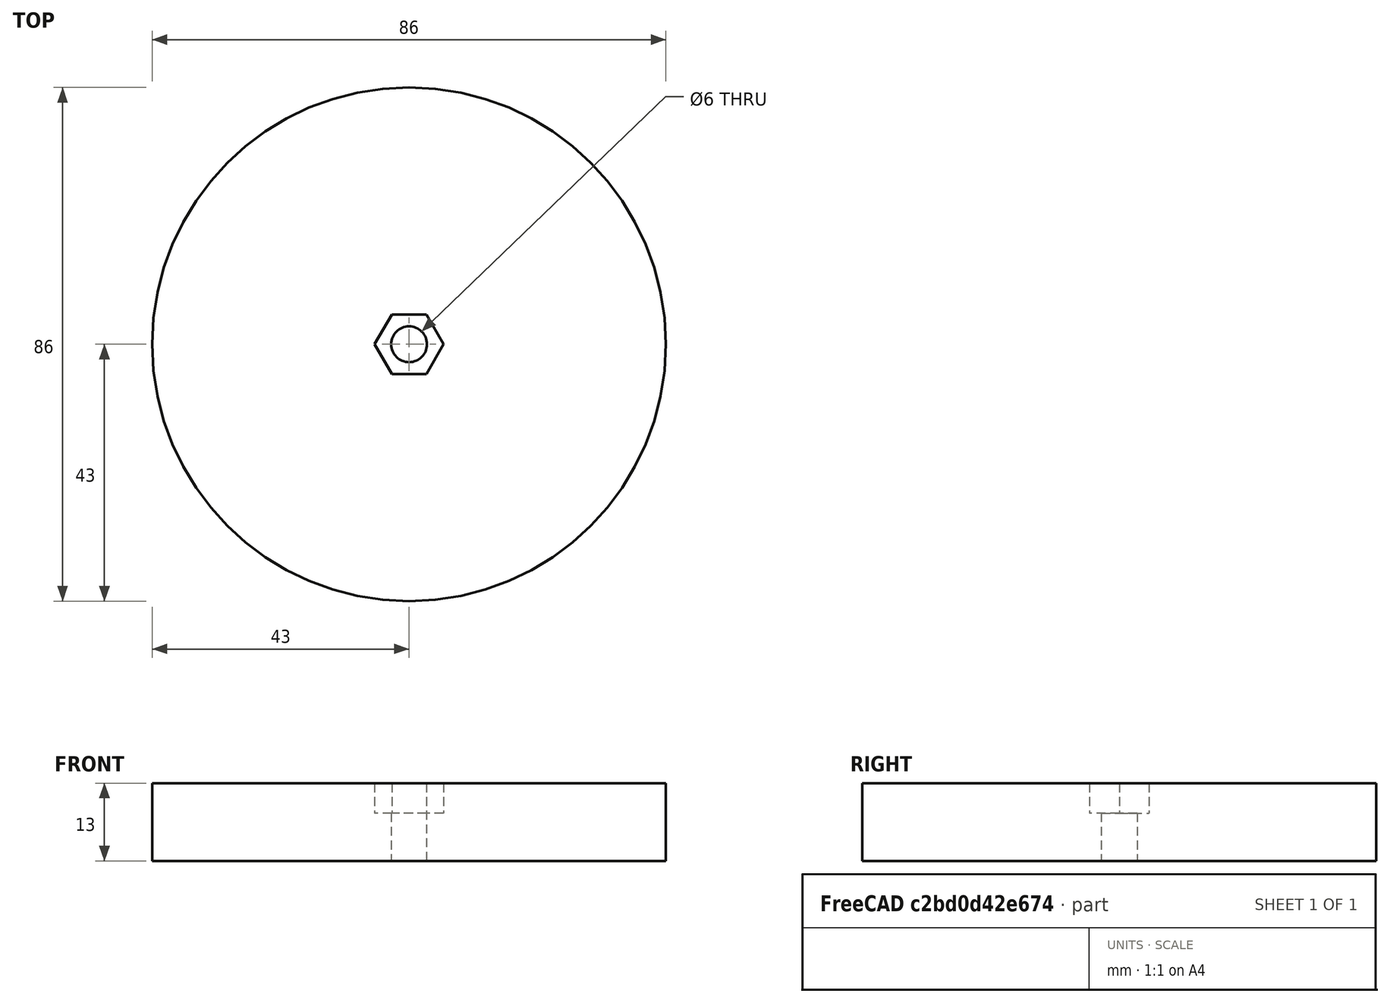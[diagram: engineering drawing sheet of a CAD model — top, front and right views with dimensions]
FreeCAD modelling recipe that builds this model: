
FCSTD DOCUMENT  (FreeCAD 0.18.4R)
Label: 12
License: All rights reserved
LicenseURL: http://en.wikipedia.org/wiki/All_rights_reserved
objects: Sketcher::SketchObject×2, PartDesign::Pad×1, PartDesign::Pocket×1, PartDesign::Body×1
note: 7 computed .brp shape members not serialized (recipe doc carries the construction recipe); baked Part::Feature solids carry a one-line shape summary decoded from their .brp

FEATURE [PartDesign::Pad] Pad  label="Unnamed"
  Length = 100
  Length2 = 100
  Type = 0
FEATURE [Sketcher::SketchObject] Sketch  label="Sketch001"
  MapMode = 5
  Placement = pos=(0,0,13) rot=(0,0,1;0rad)
  Support = -> [Pad]
  sketch-geometry (2):
    g0: Circle CenterX=0 CenterY=0 CenterZ=0 NormalX=0 NormalY=0 NormalZ=1 AngleXU=0 Radius=3
    g1: LineSegment StartX=2.88675 StartY=5 StartZ=0 EndX=-2.88675 EndY=5 EndZ=0
  constraints (4):
    c: Coincident(g0,g-1)
    c: Diameter(g0) = 86
    c: Coincident(g1,g0)
    c: Diameter(g1) = 6
FEATURE [Sketcher::SketchObject] Sketch001  label="Unnamed"
FEATURE [PartDesign::Pocket] Pocket
  BaseFeature = -> Pad
  Length = 5
  Length2 = 100
  Profile = -> Sketch001
  Type = 0
FEATURE [PartDesign::Body] Body
  Group = -> [Sketch,Pad,Sketch001,Pocket]
  Origin = -> Origin
  Tip = -> Pocket
